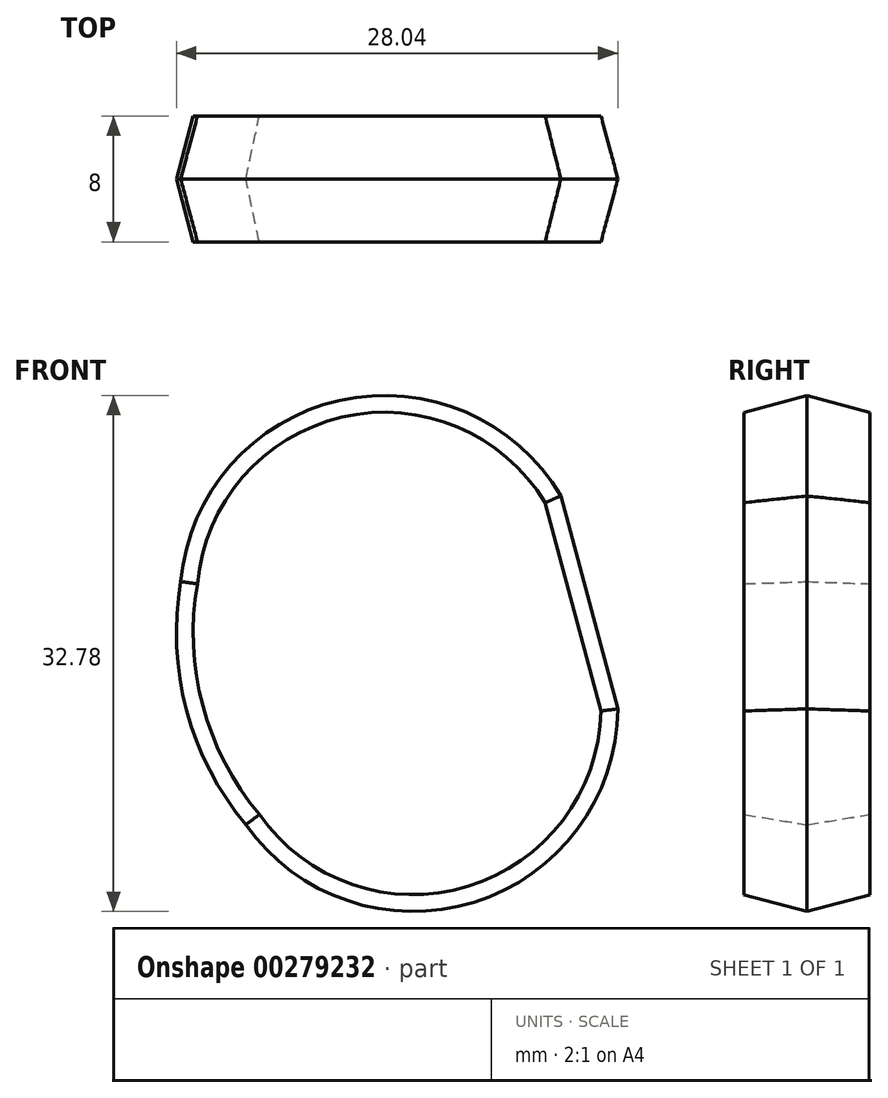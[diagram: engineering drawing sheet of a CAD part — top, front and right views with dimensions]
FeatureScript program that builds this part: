
annotation { "Feature Type Name" : "Feature", "Feature Type Description" : "" }
export const myFeature = defineFeature(function(context is Context, id is Id, definition is map)
    precondition{}
    {
        {
            var Q0;
            Q0=qCreatedBy(makeId("Front.planeOp"),FACE);
            var sketch = newSketch(context, id + "F0", { "sketchPlane" : qUnion([Q0])});
            skLineSegment(sketch, "E0", {"start": v(-27.22, 0) * mm, "end": v(82.5, 0) * mm, "construction": true});
            skLineSegment(sketch, "E1", {"start": v(83.12, 7.41) * mm, "end": v(95.18, 10.64) * mm});
            skArc(sketch, "E2", {"start": v(95.18, 10.64) * mm, "mid": v(81.13, 16.71) * mm, "end": v(71.04, 5.2) * mm});
            skArc(sketch, "E3", {"start": v(83.12, 7.41) * mm, "mid": v(82.5, 0) * mm, "end": v(86.74, -6.11) * mm});
            skLineSegment(sketch, "E4", {"start": v(86.74, -6.11) * mm, "end": v(98.8, -2.88) * mm});
            skLineSegment(sketch, "E5", {"start": v(93.13, 2.85) * mm, "end": v(67.3, -4.08) * mm, "construction": true});
            skArc(sketch, "E6.MirrorCS", {"start": v(98.8, -2.88) * mm, "mid": v(89.67, -15.16) * mm, "end": v(75.18, -10.24) * mm});
            skLineSegment(sketch, "E7", {"start": v(0, 0) * mm, "end": v(0, 15.07) * mm, "construction": true});
            skPoint(sketch, "E8.orphan", {"position": v(71.04, -6.56) * mm});
            skLineSegment(sketch, "E9", {"start": v(95.18, 10.64) * mm, "end": v(98.8, -2.88) * mm});
            skLineSegment(sketch, "E10", {"start": v(81.13, 16.71) * mm, "end": v(89.67, -15.16) * mm, "construction": true});
            skArc(sketch, "E11", {"start": v(71.04, 5.2) * mm, "mid": v(71.4, -2.97) * mm, "end": v(75.18, -10.24) * mm});
            skSolve(sketch);
        }
        {
            var Q0;
            Q0 = qSketchRegion(id + "F0", true);
            extrude(context, id + "F1", {"entities" : qUnion([Q0]), "endBound" : BoundingType.SYMMETRIC, "depth" : 8 * mm, "hasDraft" : true, "draftAngle" : 15 * degree, "draftPullDirection" : true});
        }
    });
